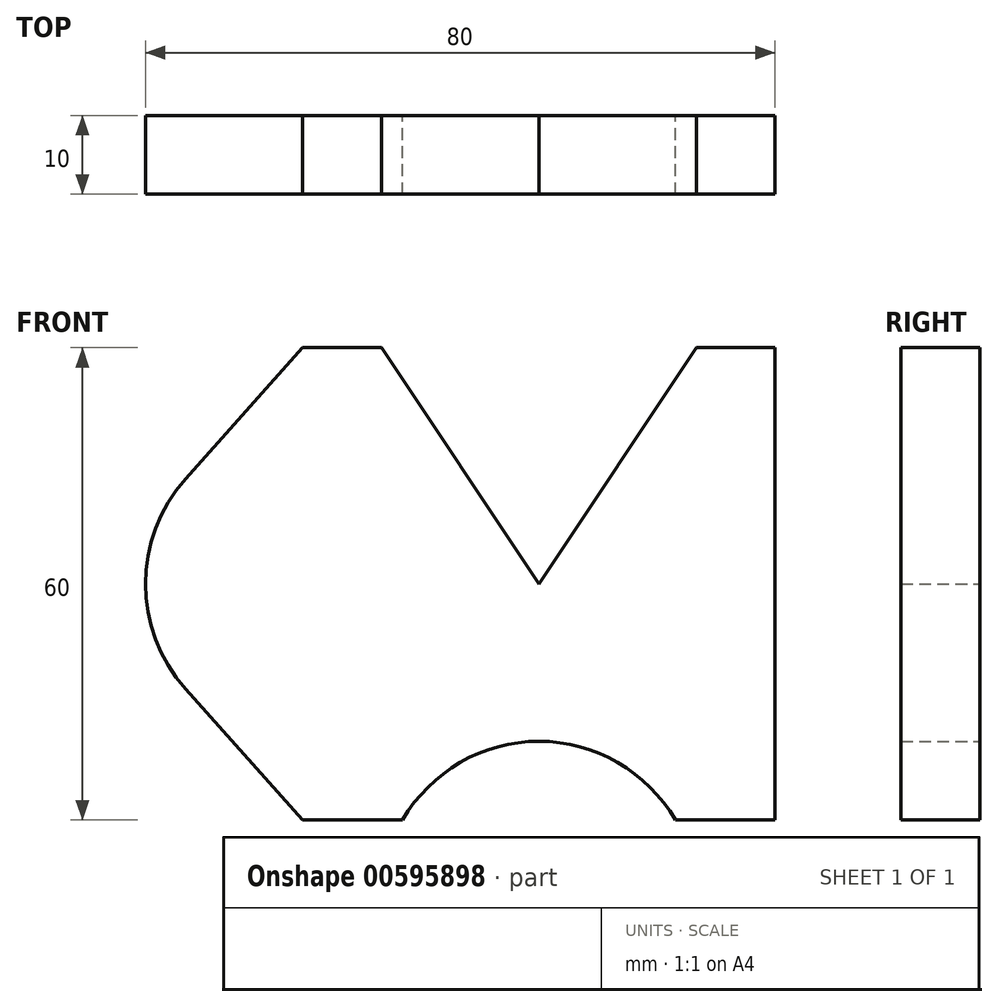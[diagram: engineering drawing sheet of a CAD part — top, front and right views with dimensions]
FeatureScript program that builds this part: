
annotation { "Feature Type Name" : "Feature", "Feature Type Description" : "" }
export const myFeature = defineFeature(function(context is Context, id is Id, definition is map)
    precondition{}
    {
        {
            var Q0;
            Q0=qCreatedBy(makeId("Front.planeOp"),FACE);
            var sketch = newSketch(context, id + "F0", { "sketchPlane" : qUnion([Q0])});
            skLineSegment(sketch, "E0", {"start": v(-30, 30) * mm, "end": v(-20, 30) * mm});
            skLineSegment(sketch, "E1", {"start": v(-20, 30) * mm, "end": v(0, 0) * mm});
            skLineSegment(sketch, "E2", {"start": v(0, 0) * mm, "end": v(20, 30) * mm});
            skLineSegment(sketch, "E3", {"start": v(20, 30) * mm, "end": v(30, 30) * mm});
            skLineSegment(sketch, "E4", {"start": v(30, 30) * mm, "end": v(30, -30) * mm});
            skLineSegment(sketch, "E5", {"start": v(30, -30) * mm, "end": v(17.32, -30) * mm});
            skLineSegment(sketch, "E6", {"start": v(-17.32, -30) * mm, "end": v(-30, -30) * mm});
            skArc(sketch, "E7", {"start": v(-44.9, 13.33) * mm, "mid": v(-50, 0) * mm, "end": v(-44.9, -13.33) * mm});
            skArc(sketch, "E8", {"start": v(17.32, -30) * mm, "mid": v(0, -20) * mm, "end": v(-17.32, -30) * mm});
            skLineSegment(sketch, "E9", {"start": v(-30, 30) * mm, "end": v(-44.9, 13.33) * mm});
            skLineSegment(sketch, "E10", {"start": v(-30, -30) * mm, "end": v(-44.9, -13.33) * mm});
            skSolve(sketch);
        }
        {
            var Q0;
            Q0=makeQuery(id+"F0.imprint","IMPRINT",FACE,{"disambiguationData":[TD([[makeQuery(id+"F0.imprint","IMPRINT",EDGE,{"derivedFrom":sQuery(id+"F0.wireOp",EDGE,"E0")}),-1.0]])]});
            extrude(context, id + "F1", {"entities" : qUnion([Q0]), "depth" : 10 * mm, "offsetDistance" : 25 * mm});
        }
    });
